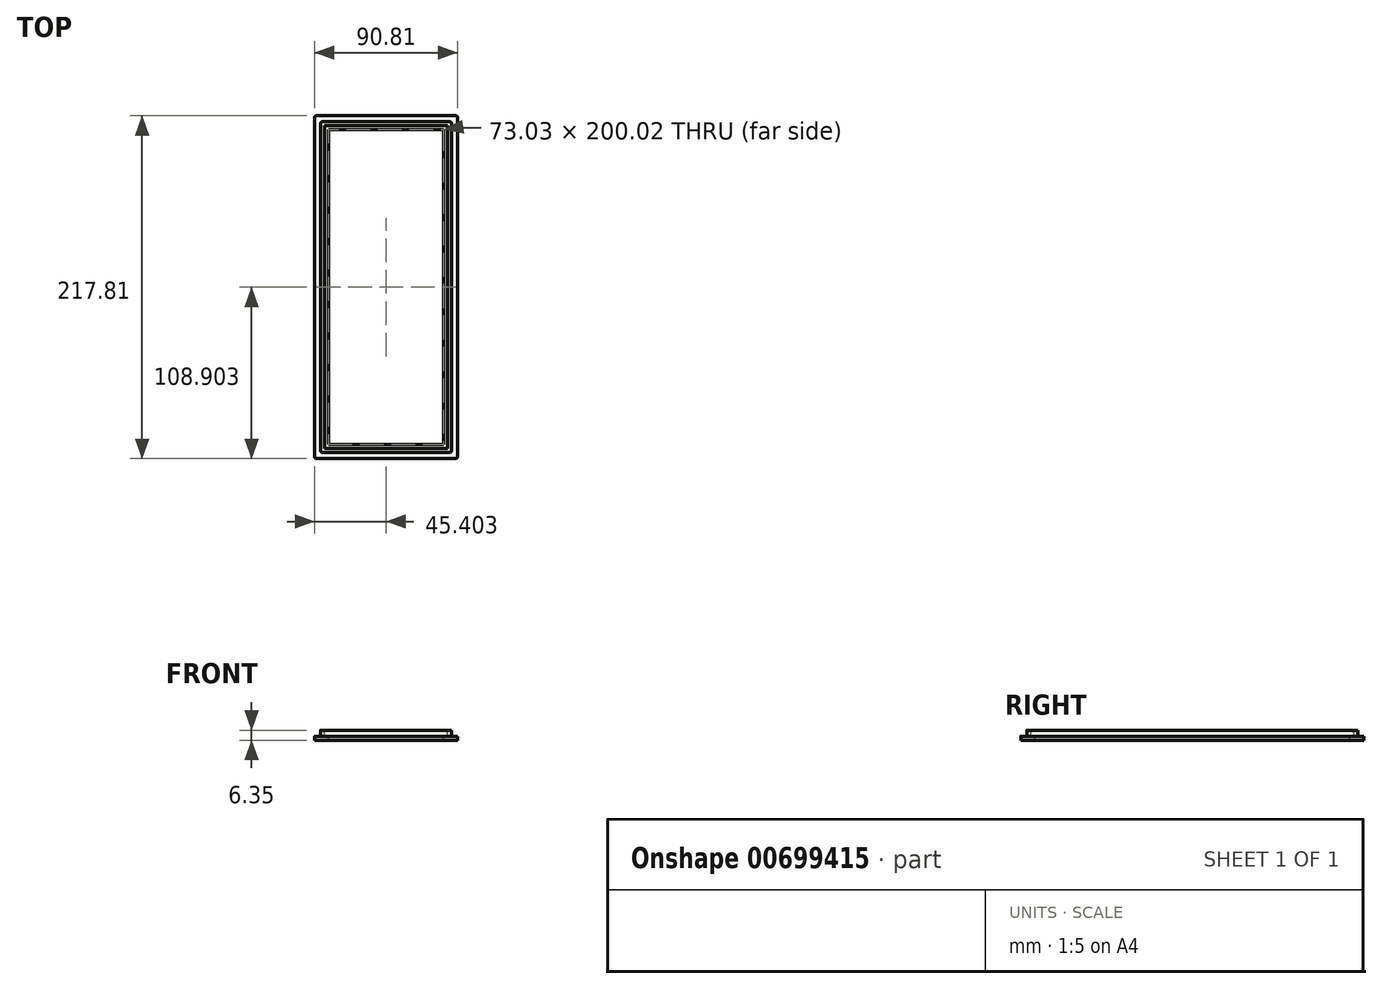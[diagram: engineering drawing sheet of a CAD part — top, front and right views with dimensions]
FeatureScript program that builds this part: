
annotation { "Feature Type Name" : "Feature", "Feature Type Description" : "" }
export const myFeature = defineFeature(function(context is Context, id is Id, definition is map)
    precondition{}
    {
        {
            var Q0;
            Q0=qCreatedBy(makeId("Top.planeOp"),FACE);
            var sketch = newSketch(context, id + "F0", { "sketchPlane" : qUnion([Q0])});
            skLineSegment(sketch, "E0.bottom", {"start": v(1.27, 0) * mm, "end": v(89.53, 0) * mm});
            skLineSegment(sketch, "E0.top", {"start": v(1.27, 217.8) * mm, "end": v(89.53, 217.8) * mm});
            skLineSegment(sketch, "E0.left", {"start": v(0, 1.27) * mm, "end": v(0, 216.53) * mm});
            skLineSegment(sketch, "E0.right", {"start": v(90.8, 1.27) * mm, "end": v(90.8, 216.53) * mm});
            skPoint(sketch, "E1.visualSharp", {"position": v(0, 217.8) * mm});
            skArc(sketch, "E1.filletArc", {"start": v(1.27, 217.8) * mm, "mid": v(0.37, 217.43) * mm, "end": v(0, 216.53) * mm});
            skPoint(sketch, "E2.visualSharp", {"position": v(90.8, 217.8) * mm});
            skArc(sketch, "E2.filletArc", {"start": v(90.8, 216.53) * mm, "mid": v(90.43, 217.43) * mm, "end": v(89.53, 217.8) * mm});
            skPoint(sketch, "E3.visualSharp", {"position": v(90.8, 0) * mm});
            skArc(sketch, "E3.filletArc", {"start": v(89.53, 0) * mm, "mid": v(90.43, 0.37) * mm, "end": v(90.8, 1.27) * mm});
            skPoint(sketch, "E4.visualSharp", {"position": v(0, 0) * mm});
            skArc(sketch, "E4.filletArc", {"start": v(0, 1.27) * mm, "mid": v(0.37, 0.37) * mm, "end": v(1.27, 0) * mm});
            skSolve(sketch);
        }
        {
            var Q0;
            Q0 = qSketchRegion(id + "F0", true);
            extrude(context, id + "F1", {"entities" : qUnion([Q0]), "depth" : 2.54 * mm, "offsetDistance" : 25.4 * mm});
        }
        {
            var Q0;
            Q0=qCreatedBy(makeId("Top.planeOp"),FACE);
            var sketch = newSketch(context, id + "F2", { "sketchPlane" : qUnion([Q0])});
            skLineSegment(sketch, "E5.0", {"start": v(3.81, 5.08) * mm, "end": v(3.81, 212.72) * mm});
            skLineSegment(sketch, "E5.1", {"start": v(5.08, 3.81) * mm, "end": v(85.73, 3.81) * mm});
            skLineSegment(sketch, "E5.2", {"start": v(87, 5.08) * mm, "end": v(87, 212.72) * mm});
            skLineSegment(sketch, "E5.3", {"start": v(5.08, 214) * mm, "end": v(85.73, 214) * mm});
            skPoint(sketch, "E6.visualSharp", {"position": v(3.81, 214) * mm});
            skArc(sketch, "E6.filletArc", {"start": v(5.08, 214) * mm, "mid": v(4.18, 213.62) * mm, "end": v(3.81, 212.72) * mm});
            skPoint(sketch, "E7.visualSharp", {"position": v(87, 214) * mm});
            skArc(sketch, "E7.filletArc", {"start": v(87, 212.72) * mm, "mid": v(86.62, 213.62) * mm, "end": v(85.73, 214) * mm});
            skPoint(sketch, "E8.visualSharp", {"position": v(87, 3.81) * mm});
            skArc(sketch, "E8.filletArc", {"start": v(85.73, 3.81) * mm, "mid": v(86.62, 4.18) * mm, "end": v(87, 5.08) * mm});
            skPoint(sketch, "E9.visualSharp", {"position": v(3.81, 3.81) * mm});
            skArc(sketch, "E9.filletArc", {"start": v(3.81, 5.08) * mm, "mid": v(4.18, 4.18) * mm, "end": v(5.08, 3.8) * mm});
            skSolve(sketch);
        }
        {
            var Q0;
            Q0 = qSketchRegion(id + "F2", true);
            extrude(context, id + "F3", {"entities" : qUnion([Q0]), "operationType" : NewBodyOperationType.ADD, "depth" : 6.35 * mm, "offsetDistance" : 25.4 * mm});
        }
        {
            var Q0;
            Q0=makeQuery(id+"F3.opExtrude","CAP_FACE",FACE,{"disambiguationData":[OSD([sQuery(id+"F2.wireOp",EDGE,"E5.0"),sQuery(id+"F2.wireOp",EDGE,"E5.1"),sQuery(id+"F2.wireOp",EDGE,"E5.2"),sQuery(id+"F2.wireOp",EDGE,"E5.3"),sQuery(id+"F2.wireOp",EDGE,"E6.filletArc"),sQuery(id+"F2.wireOp",EDGE,"E7.filletArc"),sQuery(id+"F2.wireOp",EDGE,"E8.filletArc"),sQuery(id+"F2.wireOp",EDGE,"E9.filletArc")])],"isStart":false});
            var sketch = newSketch(context, id + "F4", { "sketchPlane" : qUnion([Q0])});
            skLineSegment(sketch, "E10.0", {"start": v(6.35, 6.35) * mm, "end": v(6.35, 211.46) * mm});
            skLineSegment(sketch, "E10.1", {"start": v(6.35, 6.35) * mm, "end": v(84.46, 6.35) * mm});
            skLineSegment(sketch, "E10.2", {"start": v(84.46, 6.35) * mm, "end": v(84.46, 211.46) * mm});
            skLineSegment(sketch, "E10.3", {"start": v(6.35, 211.46) * mm, "end": v(84.46, 211.46) * mm});
            skSolve(sketch);
        }
        {
            var Q0;
            Q0 = qSketchRegion(id + "F4", true);
            extrude(context, id + "F5", {"entities" : qUnion([Q0]), "operationType" : NewBodyOperationType.REMOVE, "oppositeDirection" : true, "depth" : 3.8 * mm, "offsetDistance" : 25.4 * mm});
        }
        {
            var Q0;
            Q0=makeQuery(id+"F1.opExtrude","CAP_FACE",FACE,{"disambiguationData":[OSD([sQuery(id+"F0.wireOp",EDGE,"E0.bottom"),sQuery(id+"F0.wireOp",EDGE,"E0.top"),sQuery(id+"F0.wireOp",EDGE,"E0.left"),sQuery(id+"F0.wireOp",EDGE,"E0.right"),sQuery(id+"F0.wireOp",EDGE,"E1.filletArc"),sQuery(id+"F0.wireOp",EDGE,"E2.filletArc"),sQuery(id+"F0.wireOp",EDGE,"E3.filletArc"),sQuery(id+"F0.wireOp",EDGE,"E4.filletArc")])],"isStart":false});
            var sketch = newSketch(context, id + "F6", { "sketchPlane" : qUnion([Q0])});
            skLineSegment(sketch, "E11.0", {"start": v(8.9, 8.9) * mm, "end": v(8.9, 208.91) * mm});
            skLineSegment(sketch, "E11.1", {"start": v(8.9, 8.9) * mm, "end": v(81.91, 8.9) * mm});
            skLineSegment(sketch, "E11.2", {"start": v(81.91, 8.9) * mm, "end": v(81.91, 208.91) * mm});
            skLineSegment(sketch, "E11.3", {"start": v(8.9, 208.91) * mm, "end": v(81.91, 208.91) * mm});
            skSolve(sketch);
        }
        {
            var Q0;
            Q0 = qSketchRegion(id + "F6", true);
            extrude(context, id + "F7", {"entities" : qUnion([Q0]), "operationType" : NewBodyOperationType.REMOVE, "oppositeDirection" : true, "depth" : 2.54 * mm, "offsetDistance" : 25.4 * mm});
        }
    });
